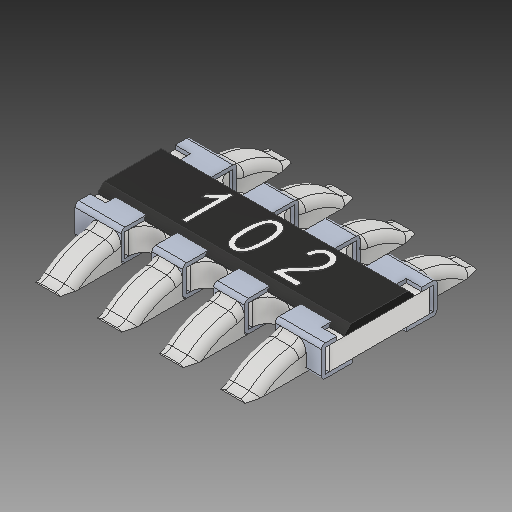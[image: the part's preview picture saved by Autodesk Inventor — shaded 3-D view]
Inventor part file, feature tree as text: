
AUTODESK INVENTOR PART (.ipt)
format: ipt  version: 2019 (Build 230136000, 136)  size: 566,272 bytes
history: native  units: in
note: dims shown in document units (in); Inventor stores cm internally (conversion verified against a paired STEP export)
features: other x8, fillet x2
ambient origin geometry x8: Origin, YZ Plane, XZ Plane, XY Plane, X Axis, Y Axis, Z Axis, Center Point
bodies: Solid1 (feature_tree), Solid2 (feature_tree), Solid3 (feature_tree), Solid4 (feature_tree), Solid5 (feature_tree), Solid6 (feature_tree), Solid7 (feature_tree), Solid8 (feature_tree), Solid9 (feature_tree), Solid10 (feature_tree)
feature tree (10):
  other  "Cut-Extrude7"
  other  "Boss-Extrude5"
  fillet  "Fillet2"  [1 undecoded]
  fillet  "Fillet1"  [1 undecoded]
  other  "LPattern3[1]"
  other  "LPattern3[2]"
  other  "LPattern3[3]"
  other  "LPattern3[4]"
  other  "LPattern3[5]"
  other  "LPattern3[6]"
note: 2 required parameter values undecoded (feature->parameter linkage not recoverable at this tier; creation-order binding heuristic only, values carry confidence <= 0.55)
